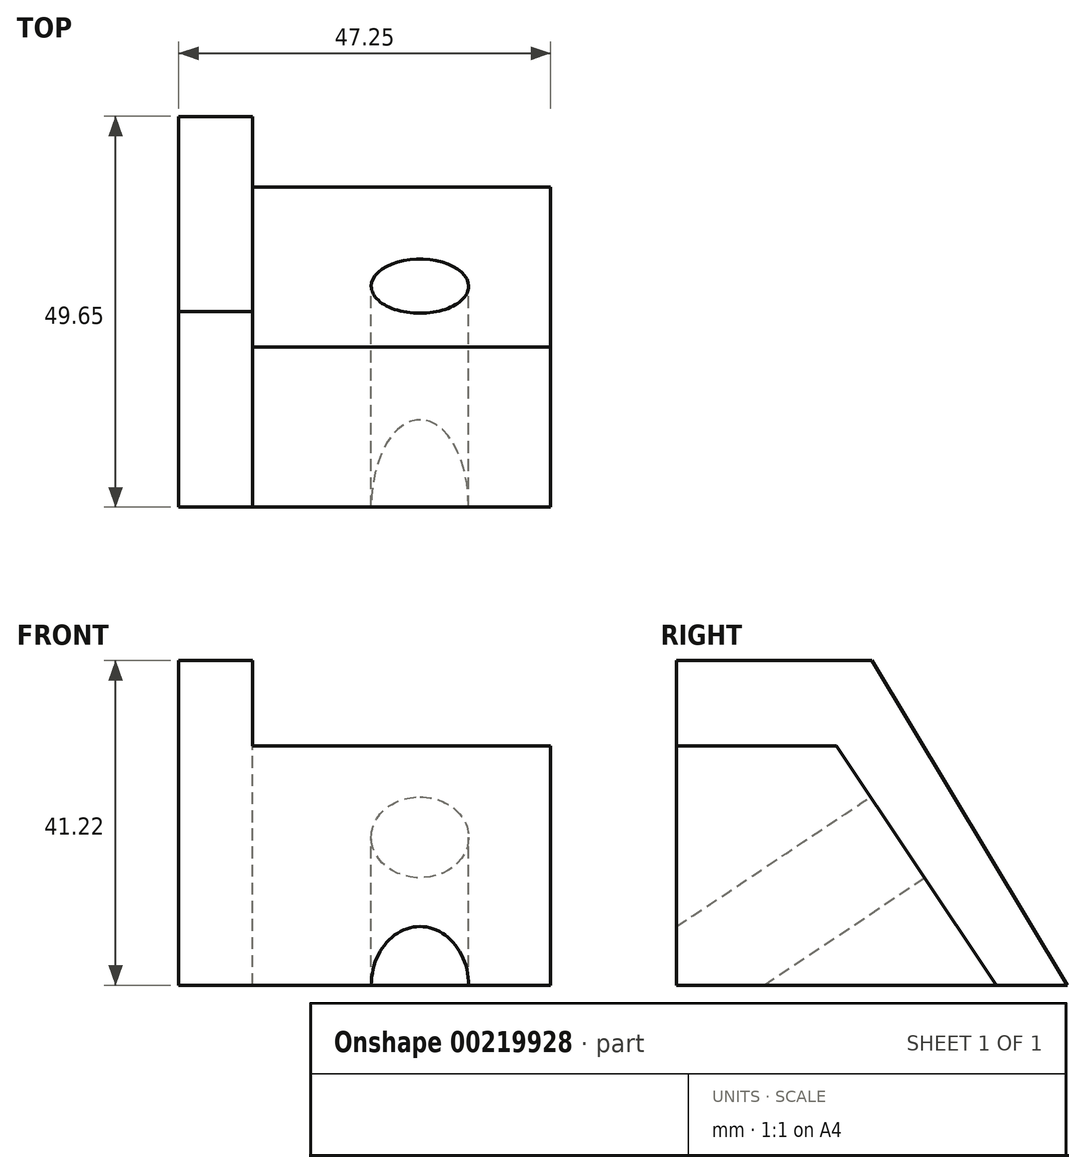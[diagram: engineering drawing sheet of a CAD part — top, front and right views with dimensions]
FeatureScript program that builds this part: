
annotation { "Feature Type Name" : "Feature", "Feature Type Description" : "" }
export const myFeature = defineFeature(function(context is Context, id is Id, definition is map)
    precondition{}
    {
        {
            var Q0;
            Q0=qCreatedBy(makeId("Right.planeOp"),FACE);
            var sketch = newSketch(context, id + "F0", { "sketchPlane" : qUnion([Q0])});
            skLineSegment(sketch, "E0", {"start": v(0, 0) * mm, "end": v(40.64, 0) * mm});
            skLineSegment(sketch, "E1", {"start": v(0, 0) * mm, "end": v(0, 30.36) * mm});
            skLineSegment(sketch, "E2", {"start": v(40.64, 0) * mm, "end": v(40.64, 30.36) * mm});
            skLineSegment(sketch, "E3", {"start": v(0, 30.36) * mm, "end": v(40.64, 30.36) * mm});
            skSolve(sketch);
        }
        {
            var Q0;
            Q0 = qSketchRegion(id + "F0", true);
            extrude(context, id + "F1", {"entities" : qUnion([Q0]), "depth" : 37.85 * mm});
        }
        {
            var Q0;
            Q0=makeQuery(id+"F1.opExtrude","CAP_FACE",FACE,{"disambiguationData":[OSD([sQuery(id+"F0.wireOp",EDGE,"E0"),sQuery(id+"F0.wireOp",EDGE,"E1"),sQuery(id+"F0.wireOp",EDGE,"E2"),sQuery(id+"F0.wireOp",EDGE,"E3")])],"isStart":true});
            var sketch = newSketch(context, id + "F2", { "sketchPlane" : qUnion([Q0])});
            skLineSegment(sketch, "E4.0", {"start": v(0, 30.36) * mm, "end": v(-40.64, 30.36) * mm});
            skLineSegment(sketch, "E5.0", {"start": v(-40.64, 0) * mm, "end": v(-40.64, 30.36) * mm});
            skLineSegment(sketch, "E6", {"start": v(-40.64, 0) * mm, "end": v(-20.32, 30.36) * mm});
            skSolve(sketch);
        }
        {
            var Q0;
            {var subQ0=sQuery(id+"F2.wireOp",EDGE,"E5.0");Q0=makeQuery(id+"F2.imprint","IMPRINT",FACE,{"disambiguationData":[TD([[makeQuery(id+"F2.imprint","IMPRINT",EDGE,{"derivedFrom":subQ0}),-1.0]])]});}
            extrude(context, id + "F3", {"entities" : qUnion([Q0]), "operationType" : NewBodyOperationType.REMOVE, "endBound" : BoundingType.THROUGH_ALL, "oppositeDirection" : true, "depth" : 25.4 * mm});
        }
        {
            var Q0;
            Q0=makeQuery(id+"F1.opExtrude","CAP_FACE",FACE,{"disambiguationData":[OSD([sQuery(id+"F0.wireOp",EDGE,"E0"),sQuery(id+"F0.wireOp",EDGE,"E1"),sQuery(id+"F0.wireOp",EDGE,"E2"),sQuery(id+"F0.wireOp",EDGE,"E3")])],"isStart":true});
            var sketch = newSketch(context, id + "F4", { "sketchPlane" : qUnion([Q0])});
            skLineSegment(sketch, "E7", {"start": v(0, 0) * mm, "end": v(0, 41.22) * mm});
            skLineSegment(sketch, "E8", {"start": v(0, 41.22) * mm, "end": v(-49.65, 41.22) * mm});
            skLineSegment(sketch, "E9", {"start": v(-49.65, 41.22) * mm, "end": v(-49.65, 0) * mm});
            skLineSegment(sketch, "E10", {"start": v(-49.65, 0) * mm, "end": v(0, 0) * mm});
            skSolve(sketch);
        }
        {
            var Q0;
            Q0 = qSketchRegion(id + "F4", true);
            extrude(context, id + "F5", {"entities" : qUnion([Q0]), "operationType" : NewBodyOperationType.ADD, "depth" : 9.4 * mm});
        }
        {
            var Q0;
            Q0=makeQuery(id+"F5.opExtrude","CAP_FACE",FACE,{"disambiguationData":[OSD([sQuery(id+"F4.wireOp",EDGE,"E7"),sQuery(id+"F4.wireOp",EDGE,"E8"),sQuery(id+"F4.wireOp",EDGE,"E9"),sQuery(id+"F4.wireOp",EDGE,"E10")])],"isStart":false});
            var sketch = newSketch(context, id + "F6", { "sketchPlane" : qUnion([Q0])});
            skLineSegment(sketch, "E11.0", {"start": v(0, 41.22) * mm, "end": v(-49.65, 41.22) * mm});
            skPoint(sketch, "E12.0", {"position": v(-49.65, 20.6) * mm});
            skLineSegment(sketch, "E13", {"start": v(-49.65, 0) * mm, "end": v(-24.82, 41.22) * mm});
            skSolve(sketch);
        }
        {
            var Q0;
            {var subQ2=sQuery(id+"F6.wireOp",EDGE,"E13");Q0=makeQuery(id+"F6.imprint","IMPRINT",FACE,{"disambiguationData":[TD([[makeQuery(id+"F6.imprint","IMPRINT",EDGE,{"derivedFrom":subQ2}),1.0]])]});}
            extrude(context, id + "F7", {"entities" : qUnion([Q0]), "operationType" : NewBodyOperationType.REMOVE, "endBound" : BoundingType.THROUGH_ALL, "oppositeDirection" : true, "depth" : 25.4 * mm});
        }
        {
            var Q0;
            Q0=makeQuery(id+"F3.boolean.opBoolean","COPY",FACE,{"derivedFrom":makeQuery(id+"F3.opExtrude","SWEPT_FACE",FACE,{"disambiguationData":[OSD([sQuery(id+"F2.wireOp",EDGE,"E6")])]})});
            var sketch = newSketch(context, id + "F8", { "sketchPlane" : qUnion([Q0])});
            skCircle(sketch, "E14", {"center": v(-21.24, 0) * mm, "radius": 6.18 * mm});
            skSolve(sketch);
        }
        {
            var Q0;
            Q0 = qSketchRegion(id + "F8", true);
            extrude(context, id + "F9", {"entities" : qUnion([Q0]), "operationType" : NewBodyOperationType.REMOVE, "endBound" : BoundingType.THROUGH_ALL, "oppositeDirection" : true, "depth" : 10.4 * mm});
        }
    });
